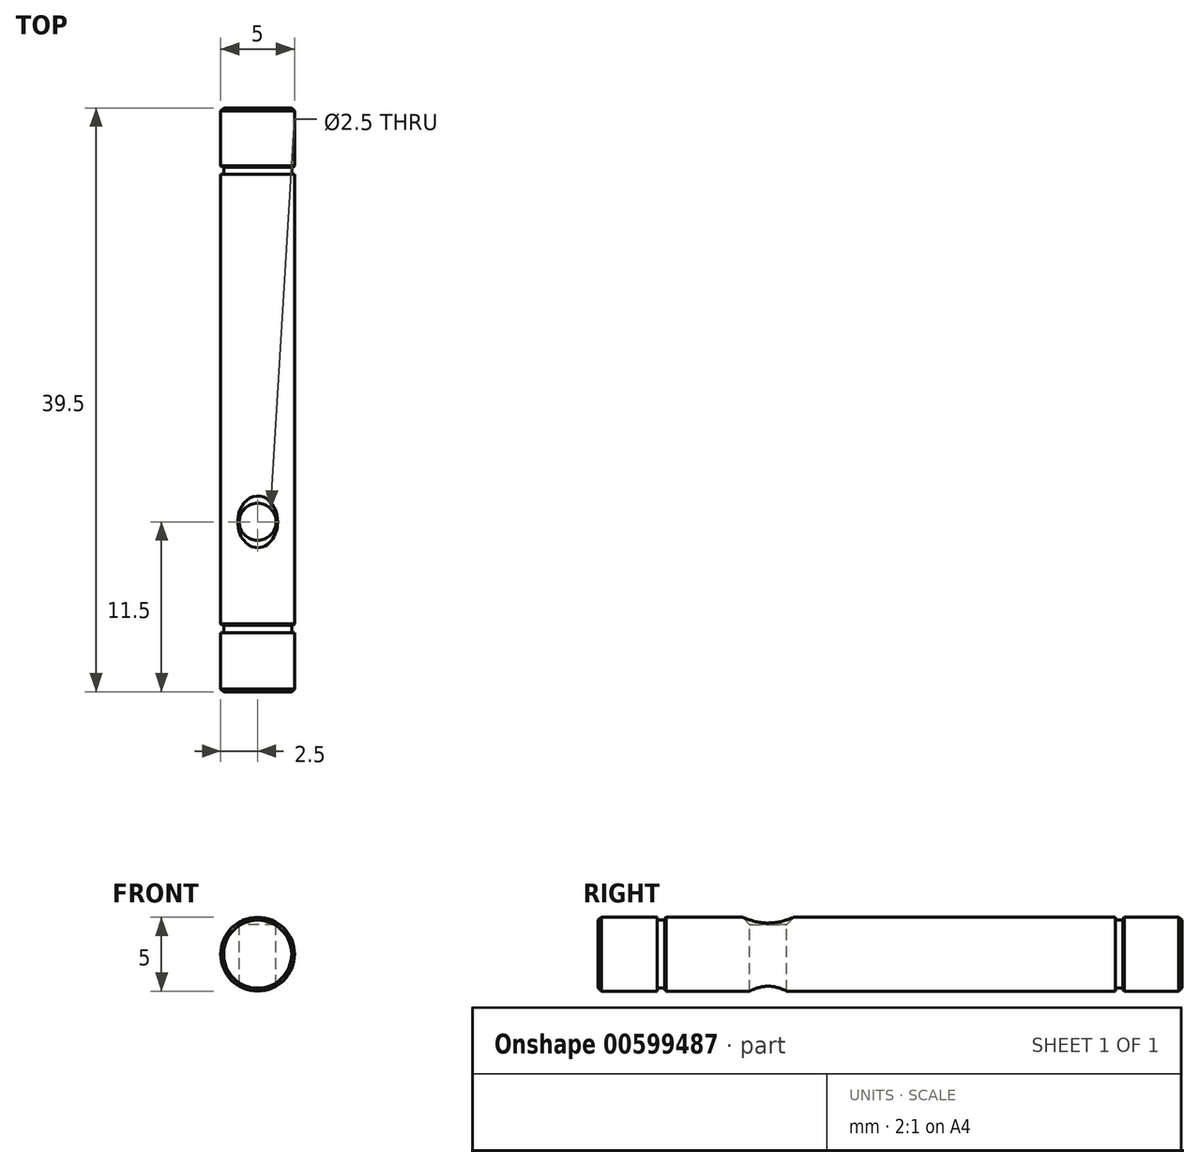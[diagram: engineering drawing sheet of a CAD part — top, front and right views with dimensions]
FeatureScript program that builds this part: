
annotation { "Feature Type Name" : "Feature", "Feature Type Description" : "" }
export const myFeature = defineFeature(function(context is Context, id is Id, definition is map)
    precondition{}
    {
        {
            var Q0;
            Q0=qCreatedBy(makeId("Front.planeOp"),FACE);
            var sketch = newSketch(context, id + "F0", { "sketchPlane" : qUnion([Q0])});
            skCircle(sketch, "E0", {"center": v(0, 0) * mm, "radius": 2.5 * mm});
            skCircle(sketch, "E1.0", {"center": v(0, 0) * mm, "radius": 2.3 * mm});
            skSolve(sketch);
        }
        {
            var Q0;
            Q0=makeQuery(id+"F0.imprint","IMPRINT",FACE,{"disambiguationData":[TD([[makeQuery(id+"F0.imprint","IMPRINT",EDGE,{"derivedFrom":sQuery(id+"F0.wireOp",EDGE,"E0")}),1.0]])]});
            var Q1;
            Q1=makeQuery(id+"F0.imprint","IMPRINT",FACE,{"disambiguationData":[TD([[makeQuery(id+"F0.imprint","IMPRINT",EDGE,{"derivedFrom":sQuery(id+"F0.wireOp",EDGE,"E1.0")}),1.0]])]});
            extrude(context, id + "F1", {"entities" : qUnion([Q0, Q1]), "depth" : 39.5 * mm, "offsetDistance" : 25 * mm});
        }
        {
            var Q0;
            Q0=qCreatedBy(makeId("Top.planeOp"),FACE);
            cPlane(context, id + "F2", {"entities" : qUnion([Q0]), "cplaneType" : CPlaneType.OFFSET, "offset" : 3 * mm, "width" : 150 * mm, "height" : 150 * mm});
        }
        {
            var Q0;
            Q0=qCreatedBy(id+"F2.planeOp",FACE);
            var sketch = newSketch(context, id + "F3", { "sketchPlane" : qUnion([Q0])});
            skPoint(sketch, "E2", {"position": v(0, -28) * mm});
            skLineSegment(sketch, "E3", {"start": v(0, 0) * mm, "end": v(0, -40.73) * mm, "construction": true});
            skSolve(sketch);
        }
        {
            var Q0;
            Q0=sQuery(id+"F3.wireOp",VERTEX,"E2");
            var Q1;
            Q1=makeQuery(id+"F1.opExtrude","SWEPT_BODY",BODY,{"disambiguationData":[OSD([sQuery(id+"F0.wireOp",EDGE,"E0")])]});
            hole(context, id + "F4", {"style" : HoleStyle.C_SINK, "endStyle" : HoleEndStyle.THROUGH, "holeDiameter" : 2.5 * mm, "cSinkDiameter" : 4.5 * mm, "cSinkAngle" : 90 * degree, "isTappedThrough" : true, "tappedDepth" : 12 * mm, "tapClearance" : 3, "startFromSketch" : true, "locations" : qUnion([Q0]), "scope" : qUnion([Q1])});
        }
        {
            var Q0;
            Q0=makeQuery(id+"F0.imprint","IMPRINT",FACE,{"disambiguationData":[TD([[makeQuery(id+"F0.imprint","IMPRINT",EDGE,{"derivedFrom":sQuery(id+"F0.wireOp",EDGE,"E0")}),1.0]])]});
            extrude(context, id + "F5", {"entities" : qUnion([Q0]), "operationType" : NewBodyOperationType.REMOVE, "depth" : 4.5 * mm, "hasSecondDirection" : true, "secondDirectionOppositeDirection" : false, "secondDirectionDepth" : 4 * mm});
        }
        {
            var Q0;
            Q0=makeQuery(id+"F1.opExtrude","CAP_FACE",FACE,{"disambiguationData":[OSD([sQuery(id+"F0.wireOp",EDGE,"E0")])],"isStart":false});
            var sketch = newSketch(context, id + "F6", { "sketchPlane" : qUnion([Q0])});
            skCircle(sketch, "E4.0", {"center": v(0, 0) * mm, "radius": 2.3 * mm});
            skSolve(sketch);
        }
        {
            var Q0;
            Q0=makeQuery(id+"F6.imprint","IMPRINT",FACE,{"disambiguationData":[TD([[makeQuery(id+"F6.imprint","IMPRINT",EDGE,{"derivedFrom":sQuery(id+"F6.wireOp",EDGE,"E4.0")}),-1.0]])]});
            extrude(context, id + "F7", {"entities" : qUnion([Q0]), "operationType" : NewBodyOperationType.REMOVE, "oppositeDirection" : true, "depth" : 4.5 * mm, "offsetDistance" : 25 * mm, "hasSecondDirection" : true, "secondDirectionOppositeDirection" : true, "secondDirectionDepth" : 4 * mm});
        }
        {
            var Q0;
            Q0=makeQuery(id+"F1.opExtrude","CAP_EDGE",EDGE,{"disambiguationData":[OSD([sQuery(id+"F0.wireOp",EDGE,"E0")])],"isStart":false});
            var Q1;
            Q1=makeQuery(id+"F1.opExtrude","CAP_EDGE",EDGE,{"disambiguationData":[OSD([sQuery(id+"F0.wireOp",EDGE,"E0")])],"isStart":true});
            chamfer(context, id + "F8", {"entities" : qUnion([Q0, Q1]), "width" : 0.2 * mm, "tangentPropagation" : true});
        }
        {
            var Q0;
            Q0=makeQuery(id+"F5.boolean.opBoolean","COPY",EDGE,{"derivedFrom":makeQuery(id+"F5.opExtrude","CAP_EDGE",EDGE,{"disambiguationData":[OSD([sQuery(id+"F0.wireOp",EDGE,"E0")])],"isStart":true})});
            var Q1;
            Q1=makeQuery(id+"F5.boolean.opBoolean","COPY",EDGE,{"derivedFrom":makeQuery(id+"F5.opExtrude","CAP_EDGE",EDGE,{"disambiguationData":[OSD([sQuery(id+"F0.wireOp",EDGE,"E0")])],"isStart":false})});
            var Q2;
            Q2=makeQuery(id+"F7.boolean.opBoolean","COPY",EDGE,{"derivedFrom":makeQuery(id+"F7.opExtrude","CAP_EDGE",EDGE,{"disambiguationData":[OSD([sQuery(id+"F0.wireOp",EDGE,"E0")])],"isStart":false})});
            var Q3;
            Q3=makeQuery(id+"F7.boolean.opBoolean","COPY",EDGE,{"derivedFrom":makeQuery(id+"F7.opExtrude","CAP_EDGE",EDGE,{"disambiguationData":[OSD([sQuery(id+"F0.wireOp",EDGE,"E0")])],"isStart":true})});
            chamfer(context, id + "F9", {"entities" : qUnion([Q0, Q1, Q2, Q3]), "width" : 0.1 * mm, "tangentPropagation" : true});
        }
    });
